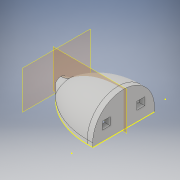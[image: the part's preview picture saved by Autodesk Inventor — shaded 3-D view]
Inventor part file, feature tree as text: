
AUTODESK INVENTOR PART (.ipt)
format: ipt  version: 2019 (Build 230136000, 136)  size: 456,704 bytes
history: native  units: in
note: dims shown in document units (in); Inventor stores cm internally (conversion verified against a paired STEP export)
features: projected_geometry x14, sketch x9, extrude x8, thicken_offset x4, plane x2, fillet x2, revolve x1
ambient origin geometry x8: Origin, YZ Plane, XZ Plane, XY Plane, X Axis, Y Axis, Z Axis, Center Point
bodies: Solid1 (feature_tree)
feature tree (40):
  revolve  "Revolution1"  [1 undecoded]
  extrude  "Extrusion2"  Depth=3.9449in
  extrude  "Extrusion3"  Depth=2.0in
  plane  "Work Plane1"
  plane  "Work Plane2"
  extrude  "Extrusion6"  Depth=0.25in
  thicken_offset  "Thicken1"
  thicken_offset  "Thicken2"
  extrude  "Extrusion7"  TaperAngle=0.0deg  [1 undecoded]
  thicken_offset  "Thicken3"
  thicken_offset  "Thicken4"
  extrude  "Extrusion8"  Depth=0.4924in
  sketch  "Sketch11"  dims[d28=0.4924in d29=0.4924in d30=0.8576in d31=0.35in]
  fillet  "Fillet1"  Radius=0.8576in
  fillet  "Fillet2"  Radius=0.35in
  extrude  "Extrusion9"  [1 undecoded]
  extrude  "Extrusion11"  TaperAngle=90.0deg  [1 undecoded]
  extrude  "Extrusion12"  Depth=0.2625in
  sketch  "Sketch3"  dims[d13=0.25in d15=1.9724in]
  sketch  "Sketch4"  dims[d16=0.25in d17=3.9449in]
  projected_geometry  "Projected Loop1"
  projected_geometry  "Projected Loop2"
  sketch  "Sketch8"  dims[d18=180.0deg d21=2.0in]
  projected_geometry  "Projected Loop10"
  projected_geometry  "Projected Loop11"
  projected_geometry  "Projected Loop12"
  sketch  "Sketch9"  dims[d23=1.0in d24=0.25in]
  sketch  "Sketch10"  dims[d26=0.25in d27=0.0in]
  projected_geometry  "Projected Loop13"
  sketch  "Sketch13"  dims[d32=0.0in d33=-4.2949in]
  projected_geometry  "Projected Loop19"
  projected_geometry  "Projected Loop20"
  projected_geometry  "Projected Loop21"
  projected_geometry  "Projected Loop22"
  sketch  "Sketch15"  dims[d38=3.945in d39=90.0deg]
  projected_geometry  "Projected Loop25"
  projected_geometry  "Projected Loop26"
  projected_geometry  "Projected Loop27"
  projected_geometry  "Projected Loop28"
  sketch  "Sketch16"  dims[d44=0.433in d45=0.683in d46=0.3415in d47=0.86in d48=0.0in d49=0.1in d50=0.1in d51=0.15in d52=0.15in d53=0.433in d54=1.4in d55=0.0in d56=0.03in d57=0.03in d58=0.1in d59=0.1in d60=0.583in d61=0.25in d62=0.0in d66=0.9361in d67=0.2625in d68=2.0in d69=0.0in d72=2.0in d73=0.0in d74=0.514in d75=2.0in d76=0.0in]
note: 4 required parameter values undecoded (feature->parameter linkage not recoverable at this tier; creation-order binding heuristic only, values carry confidence <= 0.55)